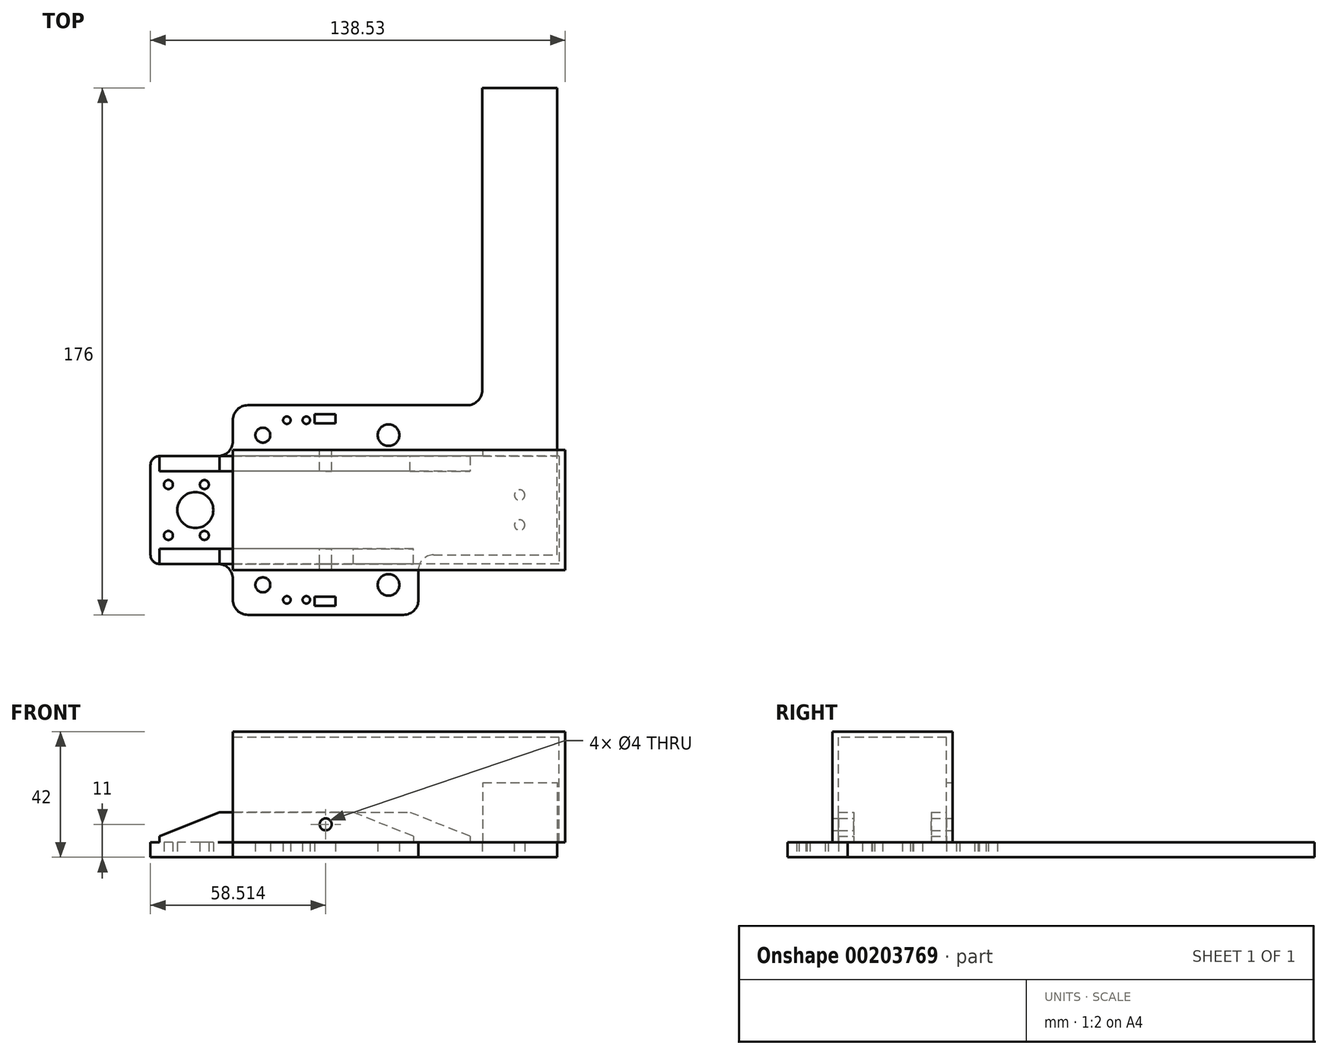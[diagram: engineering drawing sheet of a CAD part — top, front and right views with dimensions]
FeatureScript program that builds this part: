
annotation { "Feature Type Name" : "Feature", "Feature Type Description" : "" }
export const myFeature = defineFeature(function(context is Context, id is Id, definition is map)
    precondition{}
    {
        {
            var Q0;
            Q0=qCreatedBy(makeId("Top.planeOp"),FACE);
            var sketch = newSketch(context, id + "F0", { "sketchPlane" : qUnion([Q0])});
            skLineSegment(sketch, "E0.bottom", {"start": v(66.28, 35) * mm, "end": v(-17, 35) * mm});
            skLineSegment(sketch, "E0.top", {"start": v(45, -35) * mm, "end": v(-17, -35) * mm});
            skPoint(sketch, "E0.middle", {"position": v(0, 0) * mm});
            skPoint(sketch, "E1.orphan", {"position": v(-45, 35) * mm});
            skPoint(sketch, "E2.MirrorCS.end.orphan", {"position": v(-17, -35) * mm});
            skPoint(sketch, "E2.MirrorCS.start.orphan", {"position": v(-17.47, -18) * mm});
            skLineSegment(sketch, "E3", {"start": v(-17, -18) * mm, "end": v(-17, -35) * mm});
            skLineSegment(sketch, "E4", {"start": v(-44.52, 18) * mm, "end": v(-44.52, -18) * mm});
            skLineSegment(sketch, "E5", {"start": v(-44.52, -18) * mm, "end": v(-17, -18) * mm});
            skPoint(sketch, "E6.orphan", {"position": v(-45, -35) * mm});
            skLineSegment(sketch, "E7", {"start": v(45, 0) * mm, "end": v(35, 0) * mm, "construction": true});
            skLineSegment(sketch, "E8", {"start": v(35, 0) * mm, "end": v(35, 25) * mm, "construction": true});
            skCircle(sketch, "E9", {"center": v(35, 25) * mm, "radius": 3.6 * mm});
            skCircle(sketch, "E10.MirrorC", {"center": v(35, -25) * mm, "radius": 3.6 * mm});
            skLineSegment(sketch, "E11", {"start": v(35, 0) * mm, "end": v(-7, 0) * mm, "construction": true});
            skLineSegment(sketch, "E12", {"start": v(-7, 0) * mm, "end": v(-7, 25) * mm, "construction": true});
            skCircle(sketch, "E13", {"center": v(-7, 25) * mm, "radius": 2.5 * mm});
            skCircle(sketch, "E14.MirrorC", {"center": v(-7, -25) * mm, "radius": 2.5 * mm});
            skLineSegment(sketch, "E15", {"start": v(-17, -35) * mm, "end": v(-17, -40) * mm, "construction": true});
            skLineSegment(sketch, "E16", {"start": v(-17, -40) * mm, "end": v(1.04, -40) * mm, "construction": true});
            skLineSegment(sketch, "E17", {"start": v(1.04, -40) * mm, "end": v(1.04, -30) * mm, "construction": true});
            skLineSegment(sketch, "E18", {"start": v(1.04, -30) * mm, "end": v(7.54, -30) * mm, "construction": true});
            skCircle(sketch, "E19", {"center": v(1.04, -30) * mm, "radius": 1.25 * mm});
            skCircle(sketch, "E20", {"center": v(7.54, -30) * mm, "radius": 1.25 * mm});
            skLineSegment(sketch, "E21", {"start": v(45, -35) * mm, "end": v(45, -45) * mm, "construction": true});
            skLineSegment(sketch, "E22", {"start": v(45, -45) * mm, "end": v(17.28, -45) * mm, "construction": true});
            skLineSegment(sketch, "E23", {"start": v(17.28, -45) * mm, "end": v(17.28, -32) * mm, "construction": true});
            skLineSegment(sketch, "E24.bottom", {"start": v(17.28, -32) * mm, "end": v(10.28, -32) * mm});
            skLineSegment(sketch, "E24.top", {"start": v(17.28, -29) * mm, "end": v(10.28, -29) * mm});
            skLineSegment(sketch, "E24.left", {"start": v(17.28, -32) * mm, "end": v(17.28, -29) * mm});
            skLineSegment(sketch, "E24.right", {"start": v(10.28, -32) * mm, "end": v(10.28, -29) * mm});
            skLineSegment(sketch, "E25.MirrorCS", {"start": v(17.28, 32) * mm, "end": v(10.28, 32) * mm});
            skLineSegment(sketch, "E26.MirrorCS", {"start": v(17.28, 32) * mm, "end": v(17.28, 29) * mm});
            skLineSegment(sketch, "E27.MirrorCS", {"start": v(17.28, 45) * mm, "end": v(17.28, 32) * mm, "construction": true});
            skLineSegment(sketch, "E28.MirrorCS", {"start": v(17.28, 29) * mm, "end": v(10.28, 29) * mm});
            skLineSegment(sketch, "E29.MirrorCS", {"start": v(10.28, 32) * mm, "end": v(10.28, 29) * mm});
            skLineSegment(sketch, "E30", {"start": v(-44.52, 18) * mm, "end": v(-54.52, 18) * mm, "construction": true});
            skLineSegment(sketch, "E31", {"start": v(-54.52, 18) * mm, "end": v(-54.52, 0) * mm, "construction": true});
            skLineSegment(sketch, "E32", {"start": v(-54.52, 0) * mm, "end": v(-29.52, 0) * mm, "construction": true});
            skCircle(sketch, "E33", {"center": v(-29.52, 0) * mm, "radius": 6 * mm});
            skLineSegment(sketch, "E34", {"start": v(-44.52, 18) * mm, "end": v(-44.52, 28) * mm, "construction": true});
            skLineSegment(sketch, "E35", {"start": v(-44.52, 28) * mm, "end": v(-38.52, 28) * mm, "construction": true});
            skLineSegment(sketch, "E36", {"start": v(-38.52, 28) * mm, "end": v(-38.52, 8.5) * mm, "construction": true});
            skLineSegment(sketch, "E37", {"start": v(-38.52, 8.5) * mm, "end": v(-26.52, 8.5) * mm, "construction": true});
            skCircle(sketch, "E38", {"center": v(-38.52, 8.5) * mm, "radius": 1.5 * mm});
            skCircle(sketch, "E39", {"center": v(-26.52, 8.5) * mm, "radius": 1.5 * mm});
            skCircle(sketch, "E40.MirrorC", {"center": v(-38.52, -8.5) * mm, "radius": 1.5 * mm});
            skCircle(sketch, "E41.MirrorC", {"center": v(-26.52, -8.5) * mm, "radius": 1.5 * mm});
            skLineSegment(sketch, "E42", {"start": v(35, 0) * mm, "end": v(35, -7.5) * mm, "construction": true});
            skCircle(sketch, "E43.MirrorC", {"center": v(1.04, 30) * mm, "radius": 1.25 * mm});
            skCircle(sketch, "E44.MirrorC", {"center": v(7.54, 30) * mm, "radius": 1.25 * mm});
            skLineSegment(sketch, "E45", {"start": v(-17, 35) * mm, "end": v(-17, 18) * mm});
            skLineSegment(sketch, "E46", {"start": v(-44.52, 18) * mm, "end": v(-17, 18) * mm});
            skLineSegment(sketch, "E47", {"start": v(13.78, -29) * mm, "end": v(78.78, -29) * mm, "construction": true});
            skLineSegment(sketch, "E48", {"start": v(78.78, -29) * mm, "end": v(78.78, 141) * mm, "construction": true});
            skLineSegment(sketch, "E49", {"start": v(78.78, 0) * mm, "end": v(78.78, -5) * mm, "construction": true});
            skLineSegment(sketch, "E50", {"start": v(78.78, -5) * mm, "end": v(78.78, 5) * mm, "construction": true});
            skCircle(sketch, "E51", {"center": v(78.78, 5) * mm, "radius": 1.75 * mm});
            skCircle(sketch, "E52", {"center": v(78.78, -5) * mm, "radius": 1.75 * mm});
            skLineSegment(sketch, "E53.0", {"start": v(91.28, -15) * mm, "end": v(91.28, 141) * mm});
            skLineSegment(sketch, "E54.trimOffspring", {"start": v(66.28, 35) * mm, "end": v(66.28, 141) * mm});
            skLineSegment(sketch, "E55.0", {"start": v(35, -15) * mm, "end": v(-7, -15) * mm, "construction": true});
            skLineSegment(sketch, "E56", {"start": v(45, -15) * mm, "end": v(91.28, -15) * mm});
            skLineSegment(sketch, "E57.trimOffspring", {"start": v(45, -15) * mm, "end": v(45, -35) * mm});
            skPoint(sketch, "E58.orphan", {"position": v(45, 35) * mm});
            skLineSegment(sketch, "E59", {"start": v(66.28, 141) * mm, "end": v(91.28, 141) * mm});
            skSolve(sketch);
        }
        {
            var Q0;
            Q0=makeQuery(id+"F0.imprint","IMPRINT",FACE,{"disambiguationData":[TD([[makeQuery(id+"F0.imprint","IMPRINT",EDGE,{"derivedFrom":sQuery(id+"F0.wireOp",EDGE,"E0.bottom")}),1.0]])]});
            extrude(context, id + "F1", {"entities" : qUnion([Q0]), "depth" : 5 * mm, "symmetric" : true});
        }
        {
            var Q0;
            Q0=makeQuery(id+"F1.opExtrude","SWEPT_EDGE",EDGE,{"disambiguationData":[OSD([sQuery(id+"F0.wireOp",EDGE,"E0.top"),sQuery(id+"F0.wireOp",EDGE,"E0.left")])]});
            var Q1;
            Q1=makeQuery(id+"F1.opExtrude","SWEPT_EDGE",EDGE,{"disambiguationData":[OSD([sQuery(id+"F0.wireOp",EDGE,"E0.bottom"),sQuery(id+"F0.wireOp",EDGE,"E0.left")])]});
            var Q2;
            Q2=makeQuery(id+"F1.opExtrude","SWEPT_EDGE",EDGE,{"disambiguationData":[OSD([sQuery(id+"F0.wireOp",EDGE,"E0.top"),sQuery(id+"F0.wireOp",EDGE,"E3")])]});
            var Q3;
            Q3=makeQuery(id+"F1.opExtrude","SWEPT_EDGE",EDGE,{"disambiguationData":[OSD([sQuery(id+"F0.wireOp",EDGE,"E0.bottom"),sQuery(id+"F0.wireOp",EDGE,"1U8kUdJt-HrAS-oZHA-bNFJ-ENAwDHWW8smX")])]});
            fillet(context, id + "F2", {"entities" : qUnion([Q0, Q1, Q2, Q3]), "radius" : 5 * mm, "tangentPropagation" : true, "allowEdgeOverflow" : false});
        }
        {
            var Q0;
            Q0=makeQuery(id+"F1.opExtrude","SWEPT_EDGE",EDGE,{"disambiguationData":[OSD([sQuery(id+"F0.wireOp",EDGE,"P3Tx2CUv-f9ww-ONfY-XIj1-e8sIn2m9M0ST"),sQuery(id+"F0.wireOp",EDGE,"E4")])]});
            var Q1;
            Q1=makeQuery(id+"F1.opExtrude","SWEPT_EDGE",EDGE,{"disambiguationData":[OSD([sQuery(id+"F0.wireOp",EDGE,"E4"),sQuery(id+"F0.wireOp",EDGE,"E5")])]});
            fillet(context, id + "F3", {"entities" : qUnion([Q0, Q1]), "radius" : 3 * mm, "tangentPropagation" : true, "allowEdgeOverflow" : false});
        }
        {
            var Q0;
            Q0=makeQuery(id+"F1.opExtrude","SWEPT_EDGE",EDGE,{"disambiguationData":[OSD([sQuery(id+"F0.wireOp",EDGE,"E3"),sQuery(id+"F0.wireOp",EDGE,"E5")])]});
            var Q1;
            Q1=makeQuery(id+"F1.opExtrude","SWEPT_EDGE",EDGE,{"disambiguationData":[OSD([sQuery(id+"F0.wireOp",EDGE,"1U8kUdJt-HrAS-oZHA-bNFJ-ENAwDHWW8smX"),sQuery(id+"F0.wireOp",EDGE,"P3Tx2CUv-f9ww-ONfY-XIj1-e8sIn2m9M0ST")])]});
            var Q2;
            Q2=makeQuery(id+"F1.opExtrude","SWEPT_EDGE",EDGE,{"disambiguationData":[OSD([sQuery(id+"F0.wireOp",EDGE,"E56"),sQuery(id+"F0.wireOp",EDGE,"E57.trimOffspring")])]});
            var Q3;
            Q3=makeQuery(id+"F1.opExtrude","SWEPT_EDGE",EDGE,{"disambiguationData":[OSD([sQuery(id+"F0.wireOp",EDGE,"E45"),sQuery(id+"F0.wireOp",EDGE,"E46")])]});
            fillet(context, id + "F4", {"entities" : qUnion([Q0, Q1, Q2, Q3]), "radius" : 5 * mm, "tangentPropagation" : true, "allowEdgeOverflow" : false});
        }
        {
            var Q0;
            Q0=makeQuery(id+"F1.opExtrude","CAP_FACE",FACE,{"disambiguationData":[OSD([sQuery(id+"F0.wireOp",EDGE,"E0.bottom"),sQuery(id+"F0.wireOp",EDGE,"E0.top"),sQuery(id+"F0.wireOp",EDGE,"E3"),sQuery(id+"F0.wireOp",EDGE,"E4"),sQuery(id+"F0.wireOp",EDGE,"E5"),sQuery(id+"F0.wireOp",EDGE,"E9"),sQuery(id+"F0.wireOp",EDGE,"E10.MirrorC"),sQuery(id+"F0.wireOp",EDGE,"E13"),sQuery(id+"F0.wireOp",EDGE,"E14.MirrorC"),sQuery(id+"F0.wireOp",EDGE,"E19"),sQuery(id+"F0.wireOp",EDGE,"E20"),sQuery(id+"F0.wireOp",EDGE,"E24.bottom"),sQuery(id+"F0.wireOp",EDGE,"E24.top"),sQuery(id+"F0.wireOp",EDGE,"E24.left"),sQuery(id+"F0.wireOp",EDGE,"E24.right"),sQuery(id+"F0.wireOp",EDGE,"E25.MirrorCS"),sQuery(id+"F0.wireOp",EDGE,"E26.MirrorCS"),sQuery(id+"F0.wireOp",EDGE,"E28.MirrorCS"),sQuery(id+"F0.wireOp",EDGE,"E29.MirrorCS"),sQuery(id+"F0.wireOp",EDGE,"E33"),sQuery(id+"F0.wireOp",EDGE,"E38"),sQuery(id+"F0.wireOp",EDGE,"E39"),sQuery(id+"F0.wireOp",EDGE,"E40.MirrorC"),sQuery(id+"F0.wireOp",EDGE,"E41.MirrorC"),sQuery(id+"F0.wireOp",EDGE,"E43.MirrorC"),sQuery(id+"F0.wireOp",EDGE,"E44.MirrorC"),sQuery(id+"F0.wireOp",EDGE,"E45"),sQuery(id+"F0.wireOp",EDGE,"E46"),sQuery(id+"F0.wireOp",EDGE,"E51"),sQuery(id+"F0.wireOp",EDGE,"E52"),sQuery(id+"F0.wireOp",EDGE,"E53.0"),sQuery(id+"F0.wireOp",EDGE,"E54.trimOffspring"),sQuery(id+"F0.wireOp",EDGE,"E56"),sQuery(id+"F0.wireOp",EDGE,"E57.trimOffspring"),sQuery(id+"F0.wireOp",EDGE,"E59")])],"isStart":false});
            var sketch = newSketch(context, id + "F5", { "sketchPlane" : qUnion([Q0])});
            skLineSegment(sketch, "E60", {"start": v(-41.52, 18) * mm, "end": v(62.2, 18) * mm});
            skLineSegment(sketch, "E61", {"start": v(62.2, 18) * mm, "end": v(62.2, 13) * mm});
            skLineSegment(sketch, "E62", {"start": v(62.2, 13) * mm, "end": v(-41.52, 13) * mm});
            skLineSegment(sketch, "E63", {"start": v(-41.52, 13) * mm, "end": v(-41.52, 18) * mm});
            skLineSegment(sketch, "E64.MirrorCS", {"start": v(-41.52, -13) * mm, "end": v(-41.52, -18) * mm});
            skLineSegment(sketch, "E65.MirrorCS", {"start": v(-41.52, -18) * mm, "end": v(43.26, -18) * mm});
            skLineSegment(sketch, "E66.MirrorCS", {"start": v(43.26, -13) * mm, "end": v(-41.52, -13) * mm});
            skLineSegment(sketch, "E67", {"start": v(43.26, -18) * mm, "end": v(43.26, -13) * mm});
            skPoint(sketch, "E68.orphan", {"position": v(62.2, -13) * mm});
            skPoint(sketch, "E69.orphan", {"position": v(62.2, -18) * mm});
            skSolve(sketch);
        }
        {
            var Q0;
            {var subQ0=sQuery(id+"F5.wireOp",EDGE,"E61");Q0=makeQuery(id+"F5.imprint","IMPRINT",FACE,{"disambiguationData":[TD([[makeQuery(id+"F5.imprint","IMPRINT",EDGE,{"derivedFrom":subQ0}),-1.0]])]});}
            var Q1;
            {var subQ1=sQuery(id+"F5.wireOp",EDGE,"E64.MirrorCS");Q1=makeQuery(id+"F5.imprint","IMPRINT",FACE,{"disambiguationData":[TD([[makeQuery(id+"F5.imprint","IMPRINT",EDGE,{"derivedFrom":subQ1}),1.0]])]});}
            extrude(context, id + "F6", {"entities" : qUnion([Q0, Q1]), "operationType" : NewBodyOperationType.ADD, "depth" : 10 * mm, "offsetDistance" : 25 * mm});
        }
        {
            var Q0;
            Q0=makeQuery(id+"F6.opExtrude","CAP_EDGE",EDGE,{"disambiguationData":[OSD([sQuery(id+"F5.wireOp",EDGE,"E63")])],"isStart":false});
            var Q1;
            Q1=makeQuery(id+"F6.opExtrude","CAP_EDGE",EDGE,{"disambiguationData":[OSD([sQuery(id+"F5.wireOp",EDGE,"E61")])],"isStart":false});
            chamfer(context, id + "F7", {"entities" : qUnion([Q0, Q1]), "chamferType" : ChamferType.TWO_OFFSETS, "width1" : 8 * mm, "oppositeDirection" : false, "width2" : 20 * mm, "tangentPropagation" : true});
        }
        {
            var Q0;
            Q0=makeQuery(id+"F6.opExtrude","CAP_EDGE",EDGE,{"disambiguationData":[OSD([sQuery(id+"F5.wireOp",EDGE,"E64.MirrorCS")])],"isStart":false});
            var Q1;
            Q1=makeQuery(id+"F6.opExtrude","CAP_EDGE",EDGE,{"disambiguationData":[OSD([sQuery(id+"F5.wireOp",EDGE,"E67")])],"isStart":false});
            chamfer(context, id + "F8", {"entities" : qUnion([Q0, Q1]), "chamferType" : ChamferType.TWO_OFFSETS, "width1" : 20 * mm, "oppositeDirection" : false, "width2" : 8 * mm, "tangentPropagation" : true});
        }
        {
            var Q0;
            Q0=makeQuery(id+"F1.opExtrude","SWEPT_FACE",FACE,{"disambiguationData":[OSD([sQuery(id+"F0.wireOp",EDGE,"E45")])]});
            var sketch = newSketch(context, id + "F9", { "sketchPlane" : qUnion([Q0])});
            skLineSegment(sketch, "E70", {"start": v(-23, 2.5) * mm, "end": v(-18.04, 2.5) * mm, "construction": true});
            skLineSegment(sketch, "E71", {"start": v(-18.04, 2.5) * mm, "end": v(-18.04, 37.5) * mm});
            skLineSegment(sketch, "E72", {"start": v(-18.04, 37.5) * mm, "end": v(18.04, 37.5) * mm});
            skLineSegment(sketch, "E73", {"start": v(-18.04, 2.5) * mm, "end": v(-26.5, 2.5) * mm});
            skLineSegment(sketch, "E74", {"start": v(-18.04, 2.5) * mm, "end": v(-33.09, 2.5) * mm});
            skLineSegment(sketch, "E75", {"start": v(-18.04, 2.5) * mm, "end": v(-49.96, 2.5) * mm});
            skLineSegment(sketch, "E76", {"start": v(-18.04, 2.5) * mm, "end": v(-150.49, 2.5) * mm});
            skLineSegment(sketch, "E77.0", {"start": v(-20.04, 2.5) * mm, "end": v(-20.04, 39.5) * mm});
            skLineSegment(sketch, "E78", {"start": v(-18.04, 2.5) * mm, "end": v(-20.04, 2.5) * mm});
            skLineSegment(sketch, "E79.MirrorCS", {"start": v(18.04, 2.5) * mm, "end": v(20.04, 2.5) * mm});
            skLineSegment(sketch, "E80.MirrorCS", {"start": v(18.04, 2.5) * mm, "end": v(18.04, 37.5) * mm});
            skLineSegment(sketch, "E81.MirrorCS", {"start": v(20.04, 2.5) * mm, "end": v(20.04, 39.5) * mm});
            skLineSegment(sketch, "E82.0", {"start": v(-20.04, 39.5) * mm, "end": v(20.04, 39.5) * mm});
            skPoint(sketch, "E83.orphan", {"position": v(-20.04, 42.5) * mm});
            skPoint(sketch, "E84.orphan", {"position": v(20.04, 42.5) * mm});
            skSolve(sketch);
        }
        {
            var Q0;
            Q0=makeQuery(id+"F9.imprint","IMPRINT",FACE,{"disambiguationData":[TD([[makeQuery(id+"F9.imprint","IMPRINT",EDGE,{"derivedFrom":sQuery(id+"F9.wireOp",EDGE,"E71")}),1.0]])]});
            extrude(context, id + "F10", {"entities" : qUnion([Q0]), "oppositeDirection" : true, "depth" : 111 * mm, "offsetDistance" : 25 * mm});
        }
        {
            var Q0;
            Q0=makeQuery(id+"F10.opExtrude","CAP_FACE",FACE,{"disambiguationData":[OSD([sQuery(id+"F9.wireOp",EDGE,"E71"),sQuery(id+"F9.wireOp",EDGE,"E72"),sQuery(id+"F9.wireOp",EDGE,"E77.0"),sQuery(id+"F9.wireOp",EDGE,"E78"),sQuery(id+"F9.wireOp",EDGE,"E79.MirrorCS"),sQuery(id+"F9.wireOp",EDGE,"E80.MirrorCS"),sQuery(id+"F9.wireOp",EDGE,"E81.MirrorCS"),sQuery(id+"F9.wireOp",EDGE,"E82.0")])],"isStart":false});
            var sketch = newSketch(context, id + "F11", { "sketchPlane" : qUnion([Q0])});
            skLineSegment(sketch, "E85", {"start": v(-18.04, 2.5) * mm, "end": v(18.04, 2.5) * mm});
            skLineSegment(sketch, "E86", {"start": v(18.04, 2.5) * mm, "end": v(18.04, 37.5) * mm});
            skLineSegment(sketch, "E87", {"start": v(18.04, 37.5) * mm, "end": v(-18.04, 37.5) * mm});
            skLineSegment(sketch, "E88", {"start": v(-18.04, 37.5) * mm, "end": v(-18.04, 2.5) * mm});
            skSolve(sketch);
        }
        {
            var Q0;
            Q0=makeQuery(id+"F11.imprint","IMPRINT",FACE,{"disambiguationData":[TD([[makeQuery(id+"F11.imprint","IMPRINT",EDGE,{"derivedFrom":sQuery(id+"F11.wireOp",EDGE,"E85")}),1.0]])]});
            extrude(context, id + "F12", {"entities" : qUnion([Q0]), "operationType" : NewBodyOperationType.ADD, "oppositeDirection" : true, "depth" : 2 * mm, "offsetDistance" : 25 * mm});
        }
        {
            var Q0;
            Q0=makeQuery(id+"F10.opExtrude","SWEPT_FACE",FACE,{"disambiguationData":[OSD([sQuery(id+"F9.wireOp",EDGE,"E77.0")])]});
            var sketch = newSketch(context, id + "F13", { "sketchPlane" : qUnion([Q0])});
            skLineSegment(sketch, "E89", {"start": v(-91.46, 2.5) * mm, "end": v(-66.53, 2.5) * mm});
            skLineSegment(sketch, "E90", {"start": v(-66.53, 2.5) * mm, "end": v(-66.53, 22.5) * mm});
            skLineSegment(sketch, "E91", {"start": v(-66.53, 22.5) * mm, "end": v(-91.46, 22.5) * mm});
            skLineSegment(sketch, "E92", {"start": v(-91.46, 2.5) * mm, "end": v(-91.46, 22.5) * mm});
            skSolve(sketch);
        }
        {
            var Q0;
            Q0=makeQuery(id+"F13.imprint","IMPRINT",FACE,{"disambiguationData":[TD([[makeQuery(id+"F13.imprint","IMPRINT",EDGE,{"derivedFrom":sQuery(id+"F13.wireOp",EDGE,"E89")}),1.0]])]});
            extrude(context, id + "F14", {"entities" : qUnion([Q0]), "operationType" : NewBodyOperationType.REMOVE, "oppositeDirection" : true, "depth" : 2 * mm, "offsetDistance" : 25 * mm});
        }
        {
            var Q0;
            Q0=makeQuery(id+"F10.opExtrude","SWEPT_FACE",FACE,{"disambiguationData":[OSD([sQuery(id+"F9.wireOp",EDGE,"E77.0")])]});
            var sketch = newSketch(context, id + "F15", { "sketchPlane" : qUnion([Q0])});
            skLineSegment(sketch, "E93", {"start": v(-14, 2.5) * mm, "end": v(-14, 8.5) * mm, "construction": true});
            skCircle(sketch, "E94", {"center": v(-14, 8.5) * mm, "radius": 2 * mm});
            skSolve(sketch);
        }
        {
            var Q0;
            Q0=makeQuery(id+"F15.imprint","IMPRINT",FACE,{"disambiguationData":[TD([[makeQuery(id+"F15.imprint","IMPRINT",EDGE,{"derivedFrom":sQuery(id+"F15.wireOp",EDGE,"E94")}),1.0]])]});
            extrude(context, id + "F16", {"entities" : qUnion([Q0]), "operationType" : NewBodyOperationType.REMOVE, "endBound" : BoundingType.THROUGH_ALL, "oppositeDirection" : true, "depth" : 25 * mm, "offsetDistance" : 25 * mm});
        }
    });
